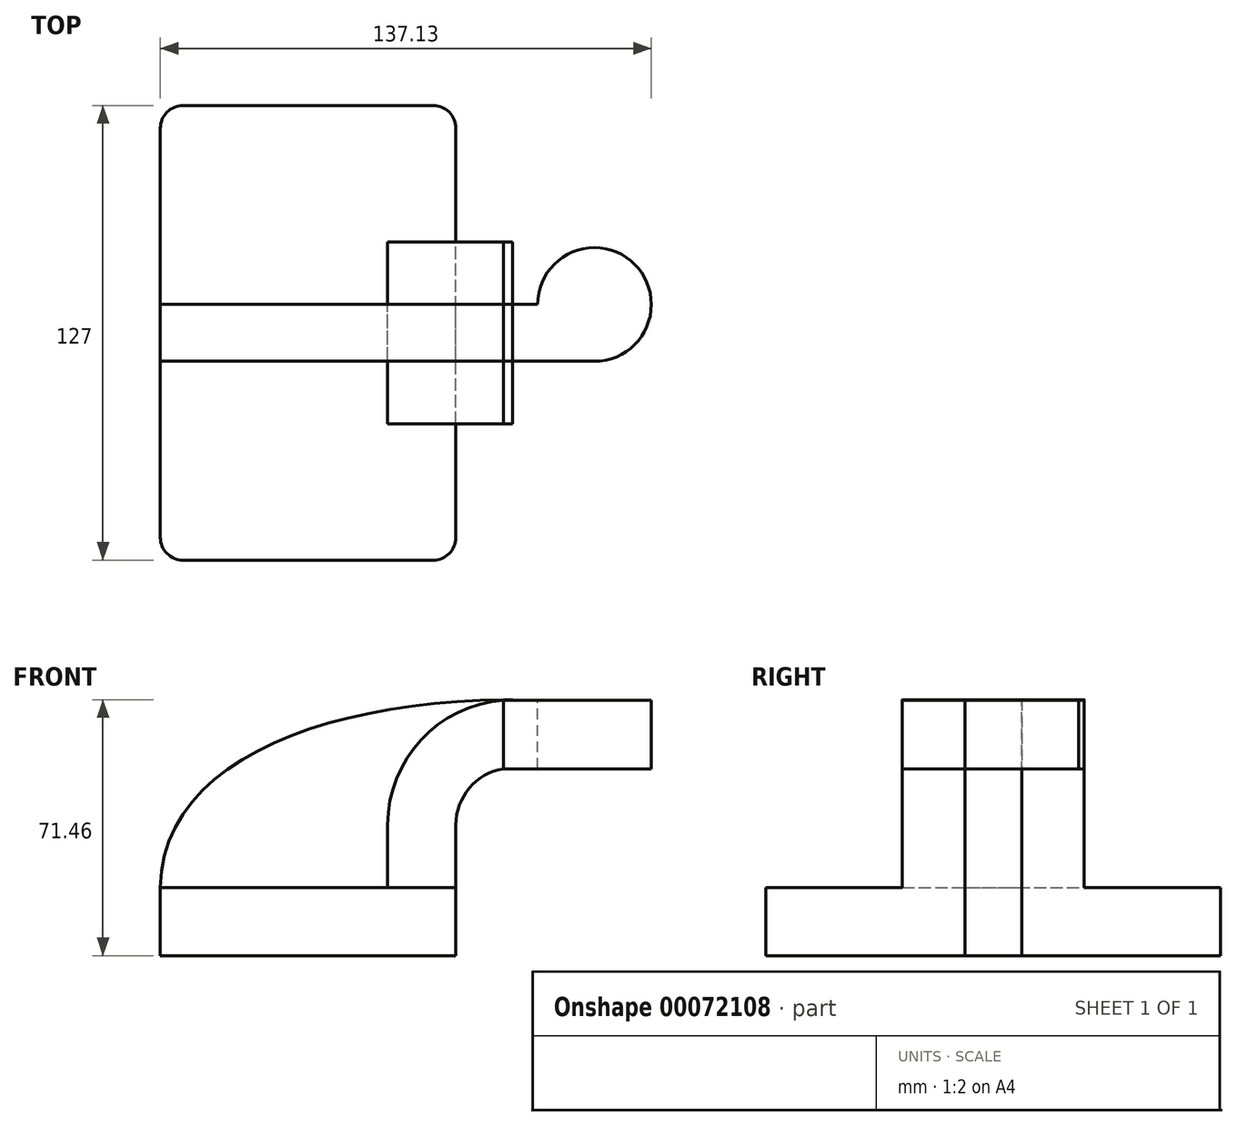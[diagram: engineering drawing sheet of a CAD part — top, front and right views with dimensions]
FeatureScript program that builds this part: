
annotation { "Feature Type Name" : "Feature", "Feature Type Description" : "" }
export const myFeature = defineFeature(function(context is Context, id is Id, definition is map)
    precondition{}
    {
        {
            var Q0;
            Q0=qCreatedBy(makeId("Front.planeOp"),FACE);
            var sketch = newSketch(context, id + "F0", { "sketchPlane" : qUnion([Q0])});
            skLineSegment(sketch, "E0.rect.bottom", {"start": v(-41.28, 9.52) * mm, "end": v(41.27, 9.53) * mm});
            skLineSegment(sketch, "E0.rect.top", {"start": v(-41.28, -9.53) * mm, "end": v(41.28, -9.53) * mm});
            skLineSegment(sketch, "E0.rect.left", {"start": v(-41.28, 9.52) * mm, "end": v(-41.27, -9.53) * mm});
            skLineSegment(sketch, "E0.rect.right", {"start": v(41.28, 9.53) * mm, "end": v(41.28, -9.52) * mm});
            skPoint(sketch, "E0.rect.middle", {"position": v(0, 0) * mm});
            skLineSegment(sketch, "E1.rect.bottom", {"start": v(54.57, 66.67) * mm, "end": v(105.37, 66.67) * mm});
            skLineSegment(sketch, "E1.rect.top", {"start": v(54.57, 38.1) * mm, "end": v(105.37, 38.1) * mm});
            skLineSegment(sketch, "E1.rect.left", {"start": v(54.57, 66.67) * mm, "end": v(54.57, 38.1) * mm});
            skLineSegment(sketch, "E1.rect.right", {"start": v(105.37, 66.67) * mm, "end": v(105.37, 38.1) * mm});
            skPoint(sketch, "E1.rect.middle", {"position": v(79.97, 52.39) * mm});
            skLineSegment(sketch, "E2", {"start": v(41.27, 9.53) * mm, "end": v(41.27, 27) * mm});
            skArc(sketch, "E3", {"start": v(41.27, 27) * mm, "mid": v(45.92, 38.23) * mm, "end": v(57.15, 42.88) * mm});
            skLineSegment(sketch, "E4", {"start": v(57.15, 42.88) * mm, "end": v(73.96, 42.88) * mm});
            skLineSegment(sketch, "E5.0", {"start": v(57.15, 61.93) * mm, "end": v(73.96, 61.93) * mm});
            skArc(sketch, "E5.1", {"start": v(22.23, 27) * mm, "mid": v(32.45, 51.7) * mm, "end": v(57.15, 61.93) * mm});
            skLineSegment(sketch, "E5.2", {"start": v(22.23, 9.53) * mm, "end": v(22.23, 27) * mm});
            skLineSegment(sketch, "E6", {"start": v(74.1, 38.1) * mm, "end": v(74.1, 66.67) * mm});
            skPoint(sketch, "E6.endSnap0", {"position": v(79.97, 66.67) * mm});
            skFitSpline(sketch, "E7", {"points": [v(-41.28, 9.52) * mm, v(57.15, 61.93) * mm], "startDerivative": vector(1.69, 107.95) * mm, "endDerivative": vector(153.5, 0.18) * mm});
            skSolve(sketch);
        }
        {
            var Q0;
            Q0=makeQuery(id+"F0.imprint","IMPRINT",FACE,{"disambiguationData":[TD([[makeQuery(id+"F0.imprint","IMPRINT",EDGE,{"derivedFrom":sQuery(id+"F0.wireOp",EDGE,"E0.rect.top")}),1.0]])]});
            extrude(context, id + "F1", {"entities" : qUnion([Q0]), "endBound" : BoundingType.SYMMETRIC, "depth" : 127 * mm});
        }
        {
            var Q0;
            Q0=makeQuery(id+"F0.imprint","IMPRINT",FACE,{"disambiguationData":[TD([[makeQuery(id+"F0.imprint","IMPRINT",EDGE,{"derivedFrom":sQuery(id+"F0.wireOp",EDGE,"E0.rect.top")}),1.0]])]});
            var Q1;
            {var subQ0=sQuery(id+"F0.wireOp",EDGE,"E7");var subQ1=sQuery(id+"F0.wireOp",EDGE,"E1.rect.left");var subQ2=makeQuery(id+"F0.imprint","INTERSECT",VERTEX,{"derivedFrom":[subQ1,subQ0]});Q1=makeQuery(id+"F0.imprint","IMPRINT",FACE,{"disambiguationData":[TD([[makeQuery(id+"F0.imprint","IMPRINT",EDGE,{"disambiguationData":[TD([[subQ2,-1.0]])],"derivedFrom":subQ1}),1.0]])]});}
            var Q2;
            {var subQ1=sQuery(id+"F0.wireOp",EDGE,"E2");Q2=makeQuery(id+"F0.imprint","IMPRINT",FACE,{"disambiguationData":[TD([[makeQuery(id+"F0.imprint","IMPRINT",EDGE,{"derivedFrom":subQ1}),1.0]])]});}
            extrude(context, id + "F2", {"entities" : qUnion([Q0, Q1, Q2]), "operationType" : NewBodyOperationType.ADD, "endBound" : BoundingType.SYMMETRIC, "depth" : 50.8 * mm});
        }
        {
            var Q0;
            Q0=makeQuery(id+"F0.imprint","IMPRINT",FACE,{"disambiguationData":[TD([[makeQuery(id+"F0.imprint","IMPRINT",EDGE,{"derivedFrom":sQuery(id+"F0.wireOp",EDGE,"E0.rect.top")}),1.0]])]});
            var Q1;
            {var subQ0=sQuery(id+"F0.wireOp",EDGE,"E7");var subQ1=sQuery(id+"F0.wireOp",EDGE,"E1.rect.left");var subQ2=makeQuery(id+"F0.imprint","INTERSECT",VERTEX,{"derivedFrom":[subQ1,subQ0]});Q1=makeQuery(id+"F0.imprint","IMPRINT",FACE,{"disambiguationData":[TD([[makeQuery(id+"F0.imprint","IMPRINT",EDGE,{"disambiguationData":[TD([[subQ2,-1.0]])],"derivedFrom":subQ1}),1.0]])]});}
            var Q2;
            {var subQ0=sQuery(id+"F0.wireOp",EDGE,"E5.2");Q2=makeQuery(id+"F0.imprint","IMPRINT",FACE,{"disambiguationData":[TD([[makeQuery(id+"F0.imprint","IMPRINT",EDGE,{"derivedFrom":subQ0}),1.0]])]});}
            var Q3;
            {var subQ1=sQuery(id+"F0.wireOp",EDGE,"E2");Q3=makeQuery(id+"F0.imprint","IMPRINT",FACE,{"disambiguationData":[TD([[makeQuery(id+"F0.imprint","IMPRINT",EDGE,{"derivedFrom":subQ1}),1.0]])]});}
            extrude(context, id + "F3", {"entities" : qUnion([Q0, Q1, Q2, Q3]), "endBound" : BoundingType.SYMMETRIC, "depth" : 15.88 * mm});
        }
        {
            var Q0;
            Q0=makeQuery(id+"F3.opExtrude","SWEPT_FACE",FACE,{"disambiguationData":[OSD([sQuery(id+"F0.wireOp",EDGE,"E1.rect.left")])]});
            extrude(context, id + "F4", {"entities" : qUnion([Q0]), "depth" : 25.4 * mm});
        }
        {
            var Q0;
            Q0=makeQuery(id+"F4.opExtrude","CAP_FACE",FACE,{"disambiguationData":[OSD([sQuery(id+"F0.wireOp",EDGE,"E1.rect.left")])],"isStart":false});
            var Q1;
            {var subQ0=sQuery(id+"F0.wireOp",EDGE,"E1.rect.left");Q1=makeQuery(id+"F4.opExtrude","CAP_EDGE",EDGE,{"disambiguationData":[OSD([subQ0]),TDD([makeQuery(id+"F3.opExtrude","CAP_EDGE",EDGE,{"disambiguationData":[OSD([subQ0])],"isStart":true})])],"isStart":false});}
            revolve(context, id + "F5", {"operationType" : NewBodyOperationType.ADD, "entities" : qUnion([Q0]), "axis" : qUnion([Q1]), "revolveType" : RevolveType.FULL});
        }
        {
            var Q0;
            Q0=makeQuery(id+"F1.opExtrude","CAP_EDGE",EDGE,{"disambiguationData":[OSD([sQuery(id+"F0.wireOp",EDGE,"E0.rect.right")])],"isStart":false});
            var Q1;
            Q1=makeQuery(id+"F1.opExtrude","CAP_EDGE",EDGE,{"disambiguationData":[OSD([sQuery(id+"F0.wireOp",EDGE,"E0.rect.left")])],"isStart":false});
            var Q2;
            Q2=makeQuery(id+"F1.opExtrude","CAP_EDGE",EDGE,{"disambiguationData":[OSD([sQuery(id+"F0.wireOp",EDGE,"E0.rect.right")])],"isStart":true});
            var Q3;
            Q3=makeQuery(id+"F1.opExtrude","CAP_EDGE",EDGE,{"disambiguationData":[OSD([sQuery(id+"F0.wireOp",EDGE,"E0.rect.left")])],"isStart":true});
            fillet(context, id + "F6", {"entities" : qUnion([Q0, Q1, Q2, Q3]), "radius" : 6.35 * mm, "tangentPropagation" : true, "allowEdgeOverflow" : false});
        }
    });
